# Revit family: Hemera_MIM_Mia-micro-suspension_R21
name_source: partatom
category: Lighting Fixtures
units: mm (PartAtom-declared; Revit-internal decimal feet)

## family parameters
Always vertical = Yes
Cut with Voids When Loaded = No
Host = Ceiling
Light Source = Yes
OmniClass Number = 23.80.70.11
OmniClass Title = Luminaries for Internal Lighting
Part Type = Normal
Room Calculation Point = No
Round Connector Dimension = Use Diameter
Shared = No

## types (240) — shared parameters
Color Filter = 16777215
Dimming Lamp Color Temperature Shift = <None>
Emit Shape Visible in Rendering = No
Emit from Circle Diameter = 50.8 mm  [stored 0.166667 ft]
HL_CanopyDiameter = 50.8 mm  [stored 0.166667 ft]
HL_CanopyHeigth = 6.35 mm  [stored 0.0208333 ft]
HL_CanopyRadius = 25.4 mm  [stored 0.0833333 ft]
HL_Frequency = 60 Hz
HL_LoadClassification = Eclairage
HL_Manufacturer = Hèmèra Inc.
HL_Model = MIA Micro-Suspension
HL_NumberofPoles = 1
HL_ProductCode = MIM
HL_URL = http://www.hemeralighting.org
Photometric Web File = MIM.IES
Tilt Angle = 90.00°
zero-valued in all types: Default Elevation

## per-type parameters (varying)
| type | HL_COC | HL_CableStart | HL_CordDiameter | HL_CylinderSize | HL_D010 | HL_FinishCable | HL_FinishCanopy | HL_FinishCylinder | HL_REM-MC |
| MIM-31-PWC-SM-COB-5W/90/35K-D010-UNV | No | 31.62 mm | 3.18 mm  [stored 0.0104331 ft] | 76.2 mm  [stored 0.25 ft] | Yes | PWC-Pearly white cord | 31-Polished nickel plated | 31-Polished nickel plated | No |
| MIM-31-PWC-MD-COB-5W/90/35K-D010-UNV | No | 31.62 mm | 3.18 mm  [stored 0.0104331 ft] | 165.1 mm  [stored 0.541667 ft] | Yes | PWC-Pearly white cord | 31-Polished nickel plated | 31-Polished nickel plated | No |
| MIM-31-PWC-LG-COB-5W/90/35K-D010-UNV | No | 31.62 mm | 3.18 mm  [stored 0.0104331 ft] | 317.5 mm | Yes | PWC-Pearly white cord | 31-Polished nickel plated | 31-Polished nickel plated | No |
| MIM-31-PWC-LG-COB-5W/90/35K-REM-MC-UNV | No | 15.88 mm  [stored 0.0520997 ft] | 3.18 mm  [stored 0.0104331 ft] | 317.5 mm | No | PWC-Pearly white cord | 31-Polished nickel plated | 31-Polished nickel plated | Yes |
| MIM-31-PWC-MD-COB-5W/90/35K-REM-MC-UNV | No | 15.88 mm  [stored 0.0520997 ft] | 3.18 mm  [stored 0.0104331 ft] | 165.1 mm  [stored 0.541667 ft] | No | PWC-Pearly white cord | 31-Polished nickel plated | 31-Polished nickel plated | Yes |
| MIM-31-PWC-SM-COB-5W/90/35K-REM-MC-UNV | No | 15.88 mm  [stored 0.0520997 ft] | 3.18 mm  [stored 0.0104331 ft] | 76.2 mm  [stored 0.25 ft] | No | PWC-Pearly white cord | 31-Polished nickel plated | 31-Polished nickel plated | Yes |
| MIM-24-SGC-SM-COB-5W/90/35K-REM-MC-UNV | No | 15.88 mm  [stored 0.0520997 ft] | 3.18 mm  [stored 0.0104331 ft] | 76.2 mm  [stored 0.25 ft] | No | SGC-Satin gold cord | 24-Brushed nickel plated | 24-Brushed nickel plated | Yes |
| MIM-24-SGC-MD-COB-5W/90/35K-REM-MC-UNV | No | 15.88 mm  [stored 0.0520997 ft] | 3.18 mm  [stored 0.0104331 ft] | 165.1 mm  [stored 0.541667 ft] | No | SGC-Satin gold cord | 24-Brushed nickel plated | 24-Brushed nickel plated | Yes |
| MIM-24-SGC-LG-COB-5W/90/35K-REM-MC-UNV | No | 15.88 mm  [stored 0.0520997 ft] | 3.18 mm  [stored 0.0104331 ft] | 317.5 mm | No | SGC-Satin gold cord | 24-Brushed nickel plated | 24-Brushed nickel plated | Yes |
| MIM-24-SGC-LG-COB-5W/90/35K-D010-UNV | No | 31.62 mm | 3.18 mm  [stored 0.0104331 ft] | 317.5 mm | Yes | SGC-Satin gold cord | 24-Brushed nickel plated | 24-Brushed nickel plated | No |
| MIM-24-SGC-MD-COB-5W/90/35K-D010-UNV | No | 31.62 mm | 3.18 mm  [stored 0.0104331 ft] | 165.1 mm  [stored 0.541667 ft] | Yes | SGC-Satin gold cord | 24-Brushed nickel plated | 24-Brushed nickel plated | No |
| MIM-24-SGC-SM-COB-5W/90/35K-D010-UNV | No | 31.62 mm | 3.18 mm  [stored 0.0104331 ft] | 76.2 mm  [stored 0.25 ft] | Yes | SGC-Satin gold cord | 24-Brushed nickel plated | 24-Brushed nickel plated | No |
| MIM-24-SBC-SM-COB-5W/90/35K-REM-MC-UNV | No | 15.88 mm  [stored 0.0520997 ft] | 3.18 mm  [stored 0.0104331 ft] | 76.2 mm  [stored 0.25 ft] | No | SBC-Silky black cord | 24-Brushed nickel plated | 24-Brushed nickel plated | Yes |
| MIM-24-SBC-MD-COB-5W/90/35K-REM-MC-UNV | No | 15.88 mm  [stored 0.0520997 ft] | 3.18 mm  [stored 0.0104331 ft] | 165.1 mm  [stored 0.541667 ft] | No | SBC-Silky black cord | 24-Brushed nickel plated | 24-Brushed nickel plated | Yes |
| MIM-24-SBC-LG-COB-5W/90/35K-REM-MC-UNV | No | 15.88 mm  [stored 0.0520997 ft] | 3.18 mm  [stored 0.0104331 ft] | 317.5 mm | No | SBC-Silky black cord | 24-Brushed nickel plated | 24-Brushed nickel plated | Yes |
| MIM-24-SBC-LG-COB-5W/90/35K-D010-UNV | No | 31.62 mm | 3.18 mm  [stored 0.0104331 ft] | 317.5 mm | Yes | SBC-Silky black cord | 24-Brushed nickel plated | 24-Brushed nickel plated | No |
| MIM-24-SBC-MD-COB-5W/90/35K-D010-UNV | No | 31.62 mm | 3.18 mm  [stored 0.0104331 ft] | 165.1 mm  [stored 0.541667 ft] | Yes | SBC-Silky black cord | 24-Brushed nickel plated | 24-Brushed nickel plated | No |
| MIM-24-SBC-SM-COB-5W/90/35K-D010-UNV | No | 31.62 mm | 3.18 mm  [stored 0.0104331 ft] | 76.2 mm  [stored 0.25 ft] | Yes | SBC-Silky black cord | 24-Brushed nickel plated | 24-Brushed nickel plated | No |
| MIM-24-COC-SM-COB-5W/90/35K-REM-MC-UNV | Yes | 15.88 mm  [stored 0.0520997 ft] | 1.59 mm  [stored 0.00521653 ft] | 76.2 mm  [stored 0.25 ft] | No | COC-Coaxial cable | 24-Brushed nickel plated | 24-Brushed nickel plated | Yes |
| MIM-24-COC-MD-COB-5W/90/35K-REM-MC-UNV | Yes | 15.88 mm  [stored 0.0520997 ft] | 1.59 mm  [stored 0.00521653 ft] | 165.1 mm  [stored 0.541667 ft] | No | COC-Coaxial cable | 24-Brushed nickel plated | 24-Brushed nickel plated | Yes |
| MIM-24-COC-LG-COB-5W/90/35K-REM-MC-UNV | Yes | 15.88 mm  [stored 0.0520997 ft] | 1.59 mm  [stored 0.00521653 ft] | 317.5 mm | No | COC-Coaxial cable | 24-Brushed nickel plated | 24-Brushed nickel plated | Yes |
| MIM-24-COC-LG-COB-5W/90/35K-D010-UNV | Yes | 31.62 mm | 1.59 mm  [stored 0.00521653 ft] | 317.5 mm | Yes | COC-Coaxial cable | 24-Brushed nickel plated | 24-Brushed nickel plated | No |
| MIM-24-COC-MD-COB-5W/90/35K-D010-UNV | Yes | 31.62 mm | 1.59 mm  [stored 0.00521653 ft] | 165.1 mm  [stored 0.541667 ft] | Yes | COC-Coaxial cable | 24-Brushed nickel plated | 24-Brushed nickel plated | No |
| MIM-24-COC-SM-COB-5W/90/35K-D010-UNV | Yes | 31.62 mm | 1.59 mm  [stored 0.00521653 ft] | 76.2 mm  [stored 0.25 ft] | Yes | COC-Coaxial cable | 24-Brushed nickel plated | 24-Brushed nickel plated | No |
| MIM-24-AGC-SM-COB-5W/90/35K-REM-MC-UNV | No | 15.88 mm  [stored 0.0520997 ft] | 3.18 mm  [stored 0.0104331 ft] | 76.2 mm  [stored 0.25 ft] | No | AGC-Anthracite gray cord | 24-Brushed nickel plated | 24-Brushed nickel plated | Yes |
| MIM-24-AGC-MD-COB-5W/90/35K-REM-MC-UNV | No | 15.88 mm  [stored 0.0520997 ft] | 3.18 mm  [stored 0.0104331 ft] | 165.1 mm  [stored 0.541667 ft] | No | AGC-Anthracite gray cord | 24-Brushed nickel plated | 24-Brushed nickel plated | Yes |
| MIM-24-AGC-LG-COB-5W/90/35K-REM-MC-UNV | No | 15.88 mm  [stored 0.0520997 ft] | 3.18 mm  [stored 0.0104331 ft] | 317.5 mm | No | AGC-Anthracite gray cord | 24-Brushed nickel plated | 24-Brushed nickel plated | Yes |
| MIM-24-AGC-LG-COB-5W/90/35K-D010-UNV | No | 31.62 mm | 3.18 mm  [stored 0.0104331 ft] | 317.5 mm | Yes | AGC-Anthracite gray cord | 24-Brushed nickel plated | 24-Brushed nickel plated | No |
| MIM-24-AGC-MD-COB-5W/90/35K-D010-UNV | No | 31.62 mm | 3.18 mm  [stored 0.0104331 ft] | 165.1 mm  [stored 0.541667 ft] | Yes | AGC-Anthracite gray cord | 24-Brushed nickel plated | 24-Brushed nickel plated | No |
| MIM-24-AGC-SM-COB-5W/90/35K-D010-UNV | No | 31.62 mm | 3.18 mm  [stored 0.0104331 ft] | 76.2 mm  [stored 0.25 ft] | Yes | AGC-Anthracite gray cord | 24-Brushed nickel plated | 24-Brushed nickel plated | No |
| MIM-24-PWC-SM-COB-5W/90/35K-REM-MC-UNV | No | 15.88 mm  [stored 0.0520997 ft] | 3.18 mm  [stored 0.0104331 ft] | 76.2 mm  [stored 0.25 ft] | No | PWC-Pearly white cord | 24-Brushed nickel plated | 24-Brushed nickel plated | Yes |
| MIM-24-PWC-MD-COB-5W/90/35K-REM-MC-UNV | No | 15.88 mm  [stored 0.0520997 ft] | 3.18 mm  [stored 0.0104331 ft] | 165.1 mm  [stored 0.541667 ft] | No | PWC-Pearly white cord | 24-Brushed nickel plated | 24-Brushed nickel plated | Yes |
| MIM-24-PWC-LG-COB-5W/90/35K-REM-MC-UNV | No | 15.88 mm  [stored 0.0520997 ft] | 3.18 mm  [stored 0.0104331 ft] | 317.5 mm | No | PWC-Pearly white cord | 24-Brushed nickel plated | 24-Brushed nickel plated | Yes |
| MIM-24-PWC-LG-COB-5W/90/35K-D010-UNV | No | 31.62 mm | 3.18 mm  [stored 0.0104331 ft] | 317.5 mm | Yes | PWC-Pearly white cord | 24-Brushed nickel plated | 24-Brushed nickel plated | No |
| MIM-24-PWC-MD-COB-5W/90/35K-D010-UNV | No | 31.62 mm | 3.18 mm  [stored 0.0104331 ft] | 165.1 mm  [stored 0.541667 ft] | Yes | PWC-Pearly white cord | 24-Brushed nickel plated | 24-Brushed nickel plated | No |
| MIM-24-PWC-SM-COB-5W/90/35K-D010-UNV | No | 31.62 mm | 3.18 mm  [stored 0.0104331 ft] | 76.2 mm  [stored 0.25 ft] | Yes | PWC-Pearly white cord | 24-Brushed nickel plated | 24-Brushed nickel plated | No |
| MIM-22-SGC-SM-COB-5W/90/35K-REM-MC-UNV | No | 15.88 mm  [stored 0.0520997 ft] | 3.18 mm  [stored 0.0104331 ft] | 76.2 mm  [stored 0.25 ft] | No | SGC-Satin gold cord | 22-Brushed gold plated | 22-Brushed gold plated | Yes |
| MIM-22-SGC-MD-COB-5W/90/35K-REM-MC-UNV | No | 15.88 mm  [stored 0.0520997 ft] | 3.18 mm  [stored 0.0104331 ft] | 165.1 mm  [stored 0.541667 ft] | No | SGC-Satin gold cord | 22-Brushed gold plated | 22-Brushed gold plated | Yes |
| MIM-22-SGC-LG-COB-5W/90/35K-REM-MC-UNV | No | 15.88 mm  [stored 0.0520997 ft] | 3.18 mm  [stored 0.0104331 ft] | 317.5 mm | No | SGC-Satin gold cord | 22-Brushed gold plated | 22-Brushed gold plated | Yes |
| MIM-22-SGC-LG-COB-5W/90/35K-D010-UNV | No | 31.62 mm | 3.18 mm  [stored 0.0104331 ft] | 317.5 mm | Yes | SGC-Satin gold cord | 22-Brushed gold plated | 22-Brushed gold plated | No |
| MIM-22-SGC-MD-COB-5W/90/35K-D010-UNV | No | 31.62 mm | 3.18 mm  [stored 0.0104331 ft] | 165.1 mm  [stored 0.541667 ft] | Yes | SGC-Satin gold cord | 22-Brushed gold plated | 22-Brushed gold plated | No |
| MIM-22-SGC-SM-COB-5W/90/35K-D010-UNV | No | 31.62 mm | 3.18 mm  [stored 0.0104331 ft] | 76.2 mm  [stored 0.25 ft] | Yes | SGC-Satin gold cord | 22-Brushed gold plated | 22-Brushed gold plated | No |
| MIM-22-SBC-SM-COB-5W/90/35K-REM-MC-UNV | No | 15.88 mm  [stored 0.0520997 ft] | 3.18 mm  [stored 0.0104331 ft] | 76.2 mm  [stored 0.25 ft] | No | SBC-Silky black cord | 22-Brushed gold plated | 22-Brushed gold plated | Yes |
| MIM-22-SBC-MD-COB-5W/90/35K-REM-MC-UNV | No | 15.88 mm  [stored 0.0520997 ft] | 3.18 mm  [stored 0.0104331 ft] | 165.1 mm  [stored 0.541667 ft] | No | SBC-Silky black cord | 22-Brushed gold plated | 22-Brushed gold plated | Yes |
| MIM-22-SBC-LG-COB-5W/90/35K-REM-MC-UNV | No | 15.88 mm  [stored 0.0520997 ft] | 3.18 mm  [stored 0.0104331 ft] | 317.5 mm | No | SBC-Silky black cord | 22-Brushed gold plated | 22-Brushed gold plated | Yes |
| MIM-22-SBC-LG-COB-5W/90/35K-D010-UNV | No | 31.62 mm | 3.18 mm  [stored 0.0104331 ft] | 317.5 mm | Yes | SBC-Silky black cord | 22-Brushed gold plated | 22-Brushed gold plated | No |
| MIM-22-SBC-MD-COB-5W/90/35K-D010-UNV | No | 31.62 mm | 3.18 mm  [stored 0.0104331 ft] | 165.1 mm  [stored 0.541667 ft] | Yes | SBC-Silky black cord | 22-Brushed gold plated | 22-Brushed gold plated | No |
| MIM-22-SBC-SM-COB-5W/90/35K-D010-UNV | No | 31.62 mm | 3.18 mm  [stored 0.0104331 ft] | 76.2 mm  [stored 0.25 ft] | Yes | SBC-Silky black cord | 22-Brushed gold plated | 22-Brushed gold plated | No |
| MIM-22-COC-SM-COB-5W/90/35K-REM-MC-UNV | Yes | 15.88 mm  [stored 0.0520997 ft] | 1.59 mm  [stored 0.00521653 ft] | 76.2 mm  [stored 0.25 ft] | No | COC-Coaxial cable | 22-Brushed gold plated | 22-Brushed gold plated | Yes |
| MIM-22-COC-MD-COB-5W/90/35K-REM-MC-UNV | Yes | 15.88 mm  [stored 0.0520997 ft] | 1.59 mm  [stored 0.00521653 ft] | 165.1 mm  [stored 0.541667 ft] | No | COC-Coaxial cable | 22-Brushed gold plated | 22-Brushed gold plated | Yes |
| MIM-22-COC-LG-COB-5W/90/35K-REM-MC-UNV | Yes | 15.88 mm  [stored 0.0520997 ft] | 1.59 mm  [stored 0.00521653 ft] | 317.5 mm | No | COC-Coaxial cable | 22-Brushed gold plated | 22-Brushed gold plated | Yes |
| MIM-22-COC-LG-COB-5W/90/35K-D010-UNV | Yes | 31.62 mm | 1.59 mm  [stored 0.00521653 ft] | 317.5 mm | Yes | COC-Coaxial cable | 22-Brushed gold plated | 22-Brushed gold plated | No |
| MIM-22-COC-MD-COB-5W/90/35K-D010-UNV | Yes | 31.62 mm | 1.59 mm  [stored 0.00521653 ft] | 165.1 mm  [stored 0.541667 ft] | Yes | COC-Coaxial cable | 22-Brushed gold plated | 22-Brushed gold plated | No |
| MIM-22-COC-SM-COB-5W/90/35K-D010-UNV | Yes | 31.62 mm | 1.59 mm  [stored 0.00521653 ft] | 76.2 mm  [stored 0.25 ft] | Yes | COC-Coaxial cable | 22-Brushed gold plated | 22-Brushed gold plated | No |
| MIM-22-AGC-SM-COB-5W/90/35K-REM-MC-UNV | No | 15.88 mm  [stored 0.0520997 ft] | 3.18 mm  [stored 0.0104331 ft] | 76.2 mm  [stored 0.25 ft] | No | AGC-Anthracite gray cord | 22-Brushed gold plated | 22-Brushed gold plated | Yes |
| MIM-22-AGC-MD-COB-5W/90/35K-REM-MC-UNV | No | 15.88 mm  [stored 0.0520997 ft] | 3.18 mm  [stored 0.0104331 ft] | 165.1 mm  [stored 0.541667 ft] | No | AGC-Anthracite gray cord | 22-Brushed gold plated | 22-Brushed gold plated | Yes |
| MIM-22-AGC-LG-COB-5W/90/35K-REM-MC-UNV | No | 15.88 mm  [stored 0.0520997 ft] | 3.18 mm  [stored 0.0104331 ft] | 317.5 mm | No | AGC-Anthracite gray cord | 22-Brushed gold plated | 22-Brushed gold plated | Yes |
| MIM-22-AGC-LG-COB-5W/90/35K-D010-UNV | No | 31.62 mm | 3.18 mm  [stored 0.0104331 ft] | 317.5 mm | Yes | AGC-Anthracite gray cord | 22-Brushed gold plated | 22-Brushed gold plated | No |
| MIM-22-AGC-MD-COB-5W/90/35K-D010-UNV | No | 31.62 mm | 3.18 mm  [stored 0.0104331 ft] | 165.1 mm  [stored 0.541667 ft] | Yes | AGC-Anthracite gray cord | 22-Brushed gold plated | 22-Brushed gold plated | No |
| MIM-22-AGC-SM-COB-5W/90/35K-D010-UNV | No | 31.62 mm | 3.18 mm  [stored 0.0104331 ft] | 76.2 mm  [stored 0.25 ft] | Yes | AGC-Anthracite gray cord | 22-Brushed gold plated | 22-Brushed gold plated | No |
| MIM-22-PWC-SM-COB-5W/90/35K-REM-MC-UNV | No | 15.88 mm  [stored 0.0520997 ft] | 3.18 mm  [stored 0.0104331 ft] | 76.2 mm  [stored 0.25 ft] | No | PWC-Pearly white cord | 22-Brushed gold plated | 22-Brushed gold plated | Yes |
| MIM-22-PWC-MD-COB-5W/90/35K-REM-MC-UNV | No | 15.88 mm  [stored 0.0520997 ft] | 3.18 mm  [stored 0.0104331 ft] | 165.1 mm  [stored 0.541667 ft] | No | PWC-Pearly white cord | 22-Brushed gold plated | 22-Brushed gold plated | Yes |
| MIM-22-PWC-LG-COB-5W/90/35K-REM-MC-UNV | No | 15.88 mm  [stored 0.0520997 ft] | 3.18 mm  [stored 0.0104331 ft] | 317.5 mm | No | PWC-Pearly white cord | 22-Brushed gold plated | 22-Brushed gold plated | Yes |
| MIM-22-PWC-LG-COB-5W/90/35K-D010-UNV | No | 31.62 mm | 3.18 mm  [stored 0.0104331 ft] | 317.5 mm | Yes | PWC-Pearly white cord | 22-Brushed gold plated | 22-Brushed gold plated | No |
| MIM-22-PWC-MD-COB-5W/90/35K-D010-UNV | No | 31.62 mm | 3.18 mm  [stored 0.0104331 ft] | 165.1 mm  [stored 0.541667 ft] | Yes | PWC-Pearly white cord | 22-Brushed gold plated | 22-Brushed gold plated | No |
| MIM-22-PWC-SM-COB-5W/90/35K-D010-UNV | No | 31.62 mm | 3.18 mm  [stored 0.0104331 ft] | 76.2 mm  [stored 0.25 ft] | Yes | PWC-Pearly white cord | 22-Brushed gold plated | 22-Brushed gold plated | No |
| MIM-21-SGC-SM-COB-5W/90/35K-REM-MC-UNV | No | 15.88 mm  [stored 0.0520997 ft] | 3.18 mm  [stored 0.0104331 ft] | 76.2 mm  [stored 0.25 ft] | No | SGC-Satin gold cord | 21-Polished gold plated | 21-Polished gold plated | Yes |
| MIM-21-SGC-MD-COB-5W/90/35K-REM-MC-UNV | No | 15.88 mm  [stored 0.0520997 ft] | 3.18 mm  [stored 0.0104331 ft] | 165.1 mm  [stored 0.541667 ft] | No | SGC-Satin gold cord | 21-Polished gold plated | 21-Polished gold plated | Yes |
| MIM-21-SGC-LG-COB-5W/90/35K-REM-MC-UNV | No | 15.88 mm  [stored 0.0520997 ft] | 3.18 mm  [stored 0.0104331 ft] | 317.5 mm | No | SGC-Satin gold cord | 21-Polished gold plated | 21-Polished gold plated | Yes |
| MIM-21-SGC-LG-COB-5W/90/35K-D010-UNV | No | 31.62 mm | 3.18 mm  [stored 0.0104331 ft] | 317.5 mm | Yes | SGC-Satin gold cord | 21-Polished gold plated | 21-Polished gold plated | No |
| MIM-21-SGC-MD-COB-5W/90/35K-D010-UNV | No | 31.62 mm | 3.18 mm  [stored 0.0104331 ft] | 165.1 mm  [stored 0.541667 ft] | Yes | SGC-Satin gold cord | 21-Polished gold plated | 21-Polished gold plated | No |
| MIM-21-SGC-SM-COB-5W/90/35K-D010-UNV | No | 31.62 mm | 3.18 mm  [stored 0.0104331 ft] | 76.2 mm  [stored 0.25 ft] | Yes | SGC-Satin gold cord | 21-Polished gold plated | 21-Polished gold plated | No |
| MIM-21-SBC-SM-COB-5W/90/35K-REM-MC-UNV | No | 15.88 mm  [stored 0.0520997 ft] | 3.18 mm  [stored 0.0104331 ft] | 76.2 mm  [stored 0.25 ft] | No | SBC-Silky black cord | 21-Polished gold plated | 21-Polished gold plated | Yes |
| MIM-21-SBC-MD-COB-5W/90/35K-REM-MC-UNV | No | 15.88 mm  [stored 0.0520997 ft] | 3.18 mm  [stored 0.0104331 ft] | 165.1 mm  [stored 0.541667 ft] | No | SBC-Silky black cord | 21-Polished gold plated | 21-Polished gold plated | Yes |
| MIM-21-SBC-LG-COB-5W/90/35K-REM-MC-UNV | No | 15.88 mm  [stored 0.0520997 ft] | 3.18 mm  [stored 0.0104331 ft] | 317.5 mm | No | SBC-Silky black cord | 21-Polished gold plated | 21-Polished gold plated | Yes |
| MIM-21-SBC-LG-COB-5W/90/35K-D010-UNV | No | 31.62 mm | 3.18 mm  [stored 0.0104331 ft] | 317.5 mm | Yes | SBC-Silky black cord | 21-Polished gold plated | 21-Polished gold plated | No |
| MIM-21-SBC-MD-COB-5W/90/35K-D010-UNV | No | 31.62 mm | 3.18 mm  [stored 0.0104331 ft] | 165.1 mm  [stored 0.541667 ft] | Yes | SBC-Silky black cord | 21-Polished gold plated | 21-Polished gold plated | No |
| MIM-21-SBC-SM-COB-5W/90/35K-D010-UNV | No | 31.62 mm | 3.18 mm  [stored 0.0104331 ft] | 76.2 mm  [stored 0.25 ft] | Yes | SBC-Silky black cord | 21-Polished gold plated | 21-Polished gold plated | No |
| MIM-21-COC-SM-COB-5W/90/35K-REM-MC-UNV | Yes | 15.88 mm  [stored 0.0520997 ft] | 1.59 mm  [stored 0.00521653 ft] | 76.2 mm  [stored 0.25 ft] | No | COC-Coaxial cable | 21-Polished gold plated | 21-Polished gold plated | Yes |
| MIM-21-COC-MD-COB-5W/90/35K-REM-MC-UNV | Yes | 15.88 mm  [stored 0.0520997 ft] | 1.59 mm  [stored 0.00521653 ft] | 165.1 mm  [stored 0.541667 ft] | No | COC-Coaxial cable | 21-Polished gold plated | 21-Polished gold plated | Yes |
| MIM-21-COC-LG-COB-5W/90/35K-REM-MC-UNV | Yes | 15.88 mm  [stored 0.0520997 ft] | 1.59 mm  [stored 0.00521653 ft] | 317.5 mm | No | COC-Coaxial cable | 21-Polished gold plated | 21-Polished gold plated | Yes |
| MIM-21-COC-LG-COB-5W/90/35K-D010-UNV | Yes | 31.62 mm | 1.59 mm  [stored 0.00521653 ft] | 317.5 mm | Yes | COC-Coaxial cable | 21-Polished gold plated | 21-Polished gold plated | No |
| MIM-21-COC-MD-COB-5W/90/35K-D010-UNV | Yes | 31.62 mm | 1.59 mm  [stored 0.00521653 ft] | 165.1 mm  [stored 0.541667 ft] | Yes | COC-Coaxial cable | 21-Polished gold plated | 21-Polished gold plated | No |
| MIM-21-COC-SM-COB-5W/90/35K-D010-UNV | Yes | 31.62 mm | 1.59 mm  [stored 0.00521653 ft] | 76.2 mm  [stored 0.25 ft] | Yes | COC-Coaxial cable | 21-Polished gold plated | 21-Polished gold plated | No |
| MIM-21-AGC-SM-COB-5W/90/35K-REM-MC-UNV | No | 15.88 mm  [stored 0.0520997 ft] | 3.18 mm  [stored 0.0104331 ft] | 76.2 mm  [stored 0.25 ft] | No | AGC-Anthracite gray cord | 21-Polished gold plated | 21-Polished gold plated | Yes |
| MIM-21-AGC-MD-COB-5W/90/35K-REM-MC-UNV | No | 15.88 mm  [stored 0.0520997 ft] | 3.18 mm  [stored 0.0104331 ft] | 165.1 mm  [stored 0.541667 ft] | No | AGC-Anthracite gray cord | 21-Polished gold plated | 21-Polished gold plated | Yes |
| MIM-21-AGC-LG-COB-5W/90/35K-REM-MC-UNV | No | 15.88 mm  [stored 0.0520997 ft] | 3.18 mm  [stored 0.0104331 ft] | 317.5 mm | No | AGC-Anthracite gray cord | 21-Polished gold plated | 21-Polished gold plated | Yes |
| MIM-21-AGC-LG-COB-5W/90/35K-D010-UNV | No | 31.62 mm | 3.18 mm  [stored 0.0104331 ft] | 317.5 mm | Yes | AGC-Anthracite gray cord | 21-Polished gold plated | 21-Polished gold plated | No |
| MIM-21-AGC-MD-COB-5W/90/35K-D010-UNV | No | 31.62 mm | 3.18 mm  [stored 0.0104331 ft] | 165.1 mm  [stored 0.541667 ft] | Yes | AGC-Anthracite gray cord | 21-Polished gold plated | 21-Polished gold plated | No |
| MIM-21-AGC-SM-COB-5W/90/35K-D010-UNV | No | 31.62 mm | 3.18 mm  [stored 0.0104331 ft] | 76.2 mm  [stored 0.25 ft] | Yes | AGC-Anthracite gray cord | 21-Polished gold plated | 21-Polished gold plated | No |
| MIM-21-PWC-SM-COB-5W/90/35K-REM-MC-UNV | No | 15.88 mm  [stored 0.0520997 ft] | 3.18 mm  [stored 0.0104331 ft] | 76.2 mm  [stored 0.25 ft] | No | PWC-Pearly white cord | 21-Polished gold plated | 21-Polished gold plated | Yes |
| MIM-21-PWC-MD-COB-5W/90/35K-REM-MC-UNV | No | 15.88 mm  [stored 0.0520997 ft] | 3.18 mm  [stored 0.0104331 ft] | 165.1 mm  [stored 0.541667 ft] | No | PWC-Pearly white cord | 21-Polished gold plated | 21-Polished gold plated | Yes |
| MIM-21-PWC-LG-COB-5W/90/35K-REM-MC-UNV | No | 15.88 mm  [stored 0.0520997 ft] | 3.18 mm  [stored 0.0104331 ft] | 317.5 mm | No | PWC-Pearly white cord | 21-Polished gold plated | 21-Polished gold plated | Yes |
| MIM-21-PWC-LG-COB-5W/90/35K-D010-UNV | No | 31.62 mm | 3.18 mm  [stored 0.0104331 ft] | 317.5 mm | Yes | PWC-Pearly white cord | 21-Polished gold plated | 21-Polished gold plated | No |
| MIM-21-PWC-MD-COB-5W/90/35K-D010-UNV | No | 31.62 mm | 3.18 mm  [stored 0.0104331 ft] | 165.1 mm  [stored 0.541667 ft] | Yes | PWC-Pearly white cord | 21-Polished gold plated | 21-Polished gold plated | No |
| MIM-21-PWC-SM-COB-5W/90/35K-D010-UNV | No | 31.62 mm | 3.18 mm  [stored 0.0104331 ft] | 76.2 mm  [stored 0.25 ft] | Yes | PWC-Pearly white cord | 21-Polished gold plated | 21-Polished gold plated | No |
| MIM-08-SGC-SM-COB-5W/90/35K-REM-MC-UNV | No | 15.88 mm  [stored 0.0520997 ft] | 3.18 mm  [stored 0.0104331 ft] | 76.2 mm  [stored 0.25 ft] | No | SGC-Satin gold cord | 08-Dark mat bronze painted | 08-Dark mat bronze painted | Yes |
| MIM-08-SGC-MD-COB-5W/90/35K-REM-MC-UNV | No | 15.88 mm  [stored 0.0520997 ft] | 3.18 mm  [stored 0.0104331 ft] | 165.1 mm  [stored 0.541667 ft] | No | SGC-Satin gold cord | 08-Dark mat bronze painted | 08-Dark mat bronze painted | Yes |
| MIM-08-SGC-LG-COB-5W/90/35K-REM-MC-UNV | No | 15.88 mm  [stored 0.0520997 ft] | 3.18 mm  [stored 0.0104331 ft] | 317.5 mm | No | SGC-Satin gold cord | 08-Dark mat bronze painted | 08-Dark mat bronze painted | Yes |
| MIM-08-SGC-LG-COB-5W/90/35K-D010-UNV | No | 31.62 mm | 3.18 mm  [stored 0.0104331 ft] | 317.5 mm | Yes | SGC-Satin gold cord | 08-Dark mat bronze painted | 08-Dark mat bronze painted | No |
| MIM-08-SGC-MD-COB-5W/90/35K-D010-UNV | No | 31.62 mm | 3.18 mm  [stored 0.0104331 ft] | 165.1 mm  [stored 0.541667 ft] | Yes | SGC-Satin gold cord | 08-Dark mat bronze painted | 08-Dark mat bronze painted | No |
| MIM-08-SGC-SM-COB-5W/90/35K-D010-UNV | No | 31.62 mm | 3.18 mm  [stored 0.0104331 ft] | 76.2 mm  [stored 0.25 ft] | Yes | SGC-Satin gold cord | 08-Dark mat bronze painted | 08-Dark mat bronze painted | No |
| MIM-08-SBC-SM-COB-5W/90/35K-REM-MC-UNV | No | 15.88 mm  [stored 0.0520997 ft] | 3.18 mm  [stored 0.0104331 ft] | 76.2 mm  [stored 0.25 ft] | No | SBC-Silky black cord | 08-Dark mat bronze painted | 08-Dark mat bronze painted | Yes |
| MIM-08-SBC-MD-COB-5W/90/35K-REM-MC-UNV | No | 15.88 mm  [stored 0.0520997 ft] | 3.18 mm  [stored 0.0104331 ft] | 165.1 mm  [stored 0.541667 ft] | No | SBC-Silky black cord | 08-Dark mat bronze painted | 08-Dark mat bronze painted | Yes |
| MIM-08-SBC-LG-COB-5W/90/35K-REM-MC-UNV | No | 15.88 mm  [stored 0.0520997 ft] | 3.18 mm  [stored 0.0104331 ft] | 317.5 mm | No | SBC-Silky black cord | 08-Dark mat bronze painted | 08-Dark mat bronze painted | Yes |
| MIM-08-SBC-LG-COB-5W/90/35K-D010-UNV | No | 31.62 mm | 3.18 mm  [stored 0.0104331 ft] | 317.5 mm | Yes | SBC-Silky black cord | 08-Dark mat bronze painted | 08-Dark mat bronze painted | No |
| MIM-08-SBC-MD-COB-5W/90/35K-D010-UNV | No | 31.62 mm | 3.18 mm  [stored 0.0104331 ft] | 165.1 mm  [stored 0.541667 ft] | Yes | SBC-Silky black cord | 08-Dark mat bronze painted | 08-Dark mat bronze painted | No |
| MIM-08-SBC-SM-COB-5W/90/35K-D010-UNV | No | 31.62 mm | 3.18 mm  [stored 0.0104331 ft] | 76.2 mm  [stored 0.25 ft] | Yes | SBC-Silky black cord | 08-Dark mat bronze painted | 08-Dark mat bronze painted | No |
| MIM-08-COC-SM-COB-5W/90/35K-REM-MC-UNV | Yes | 15.88 mm  [stored 0.0520997 ft] | 1.59 mm  [stored 0.00521653 ft] | 76.2 mm  [stored 0.25 ft] | No | COC-Coaxial cable | 08-Dark mat bronze painted | 08-Dark mat bronze painted | Yes |
| MIM-08-COC-MD-COB-5W/90/35K-REM-MC-UNV | Yes | 15.88 mm  [stored 0.0520997 ft] | 1.59 mm  [stored 0.00521653 ft] | 165.1 mm  [stored 0.541667 ft] | No | COC-Coaxial cable | 08-Dark mat bronze painted | 08-Dark mat bronze painted | Yes |
| MIM-08-COC-LG-COB-5W/90/35K-REM-MC-UNV | Yes | 15.88 mm  [stored 0.0520997 ft] | 1.59 mm  [stored 0.00521653 ft] | 317.5 mm | No | COC-Coaxial cable | 08-Dark mat bronze painted | 08-Dark mat bronze painted | Yes |
| MIM-08-COC-LG-COB-5W/90/35K-D010-UNV | Yes | 31.62 mm | 1.59 mm  [stored 0.00521653 ft] | 317.5 mm | Yes | COC-Coaxial cable | 08-Dark mat bronze painted | 08-Dark mat bronze painted | No |
| MIM-08-COC-MD-COB-5W/90/35K-D010-UNV | Yes | 31.62 mm | 1.59 mm  [stored 0.00521653 ft] | 165.1 mm  [stored 0.541667 ft] | Yes | COC-Coaxial cable | 08-Dark mat bronze painted | 08-Dark mat bronze painted | No |
| MIM-08-COC-SM-COB-5W/90/35K-D010-UNV | Yes | 31.62 mm | 1.59 mm  [stored 0.00521653 ft] | 76.2 mm  [stored 0.25 ft] | Yes | COC-Coaxial cable | 08-Dark mat bronze painted | 08-Dark mat bronze painted | No |
| MIM-08-AGC-SM-COB-5W/90/35K-REM-MC-UNV | No | 15.88 mm  [stored 0.0520997 ft] | 3.18 mm  [stored 0.0104331 ft] | 76.2 mm  [stored 0.25 ft] | No | AGC-Anthracite gray cord | 08-Dark mat bronze painted | 08-Dark mat bronze painted | Yes |
| MIM-08-AGC-MD-COB-5W/90/35K-REM-MC-UNV | No | 15.88 mm  [stored 0.0520997 ft] | 3.18 mm  [stored 0.0104331 ft] | 165.1 mm  [stored 0.541667 ft] | No | AGC-Anthracite gray cord | 08-Dark mat bronze painted | 08-Dark mat bronze painted | Yes |
| MIM-08-AGC-LG-COB-5W/90/35K-REM-MC-UNV | No | 15.88 mm  [stored 0.0520997 ft] | 3.18 mm  [stored 0.0104331 ft] | 317.5 mm | No | AGC-Anthracite gray cord | 08-Dark mat bronze painted | 08-Dark mat bronze painted | Yes |
| MIM-08-AGC-LG-COB-5W/90/35K-D010-UNV | No | 31.62 mm | 3.18 mm  [stored 0.0104331 ft] | 317.5 mm | Yes | AGC-Anthracite gray cord | 08-Dark mat bronze painted | 08-Dark mat bronze painted | No |
| MIM-08-AGC-MD-COB-5W/90/35K-D010-UNV | No | 31.62 mm | 3.18 mm  [stored 0.0104331 ft] | 165.1 mm  [stored 0.541667 ft] | Yes | AGC-Anthracite gray cord | 08-Dark mat bronze painted | 08-Dark mat bronze painted | No |
| MIM-08-AGC-SM-COB-5W/90/35K-D010-UNV | No | 31.62 mm | 3.18 mm  [stored 0.0104331 ft] | 76.2 mm  [stored 0.25 ft] | Yes | AGC-Anthracite gray cord | 08-Dark mat bronze painted | 08-Dark mat bronze painted | No |
| MIM-08-PWC-SM-COB-5W/90/35K-REM-MC-UNV | No | 15.88 mm  [stored 0.0520997 ft] | 3.18 mm  [stored 0.0104331 ft] | 76.2 mm  [stored 0.25 ft] | No | PWC-Pearly white cord | 08-Dark mat bronze painted | 08-Dark mat bronze painted | Yes |
| MIM-08-PWC-MD-COB-5W/90/35K-REM-MC-UNV | No | 15.88 mm  [stored 0.0520997 ft] | 3.18 mm  [stored 0.0104331 ft] | 165.1 mm  [stored 0.541667 ft] | No | PWC-Pearly white cord | 08-Dark mat bronze painted | 08-Dark mat bronze painted | Yes |
| MIM-08-PWC-LG-COB-5W/90/35K-REM-MC-UNV | No | 15.88 mm  [stored 0.0520997 ft] | 3.18 mm  [stored 0.0104331 ft] | 317.5 mm | No | PWC-Pearly white cord | 08-Dark mat bronze painted | 08-Dark mat bronze painted | Yes |
| MIM-08-PWC-LG-COB-5W/90/35K-D010-UNV | No | 31.62 mm | 3.18 mm  [stored 0.0104331 ft] | 317.5 mm | Yes | PWC-Pearly white cord | 08-Dark mat bronze painted | 08-Dark mat bronze painted | No |
| MIM-08-PWC-MD-COB-5W/90/35K-D010-UNV | No | 31.62 mm | 3.18 mm  [stored 0.0104331 ft] | 165.1 mm  [stored 0.541667 ft] | Yes | PWC-Pearly white cord | 08-Dark mat bronze painted | 08-Dark mat bronze painted | No |
| MIM-08-PWC-SM-COB-5W/90/35K-D010-UNV | No | 31.62 mm | 3.18 mm  [stored 0.0104331 ft] | 76.2 mm  [stored 0.25 ft] | Yes | PWC-Pearly white cord | 08-Dark mat bronze painted | 08-Dark mat bronze painted | No |
| MIM-03-SGC-SM-COB-5W/90/35K-REM-MC-UNV | No | 15.88 mm  [stored 0.0520997 ft] | 3.18 mm  [stored 0.0104331 ft] | 76.2 mm  [stored 0.25 ft] | No | SGC-Satin gold cord | 03-Warm dark grey painted | 03-Warm dark grey painted | Yes |
| MIM-03-SGC-MD-COB-5W/90/35K-REM-MC-UNV | No | 15.88 mm  [stored 0.0520997 ft] | 3.18 mm  [stored 0.0104331 ft] | 165.1 mm  [stored 0.541667 ft] | No | SGC-Satin gold cord | 03-Warm dark grey painted | 03-Warm dark grey painted | Yes |
| MIM-03-SGC-LG-COB-5W/90/35K-REM-MC-UNV | No | 15.88 mm  [stored 0.0520997 ft] | 3.18 mm  [stored 0.0104331 ft] | 317.5 mm | No | SGC-Satin gold cord | 03-Warm dark grey painted | 03-Warm dark grey painted | Yes |
| MIM-03-SGC-LG-COB-5W/90/35K-D010-UNV | No | 31.62 mm | 3.18 mm  [stored 0.0104331 ft] | 317.5 mm | Yes | SGC-Satin gold cord | 03-Warm dark grey painted | 03-Warm dark grey painted | No |
| MIM-03-SGC-MD-COB-5W/90/35K-D010-UNV | No | 31.62 mm | 3.18 mm  [stored 0.0104331 ft] | 165.1 mm  [stored 0.541667 ft] | Yes | SGC-Satin gold cord | 03-Warm dark grey painted | 03-Warm dark grey painted | No |
| MIM-03-SGC-SM-COB-5W/90/35K-D010-UNV | No | 31.62 mm | 3.18 mm  [stored 0.0104331 ft] | 76.2 mm  [stored 0.25 ft] | Yes | SGC-Satin gold cord | 03-Warm dark grey painted | 03-Warm dark grey painted | No |
| MIM-03-SBC-SM-COB-5W/90/35K-REM-MC-UNV | No | 15.88 mm  [stored 0.0520997 ft] | 3.18 mm  [stored 0.0104331 ft] | 76.2 mm  [stored 0.25 ft] | No | SBC-Silky black cord | 03-Warm dark grey painted | 03-Warm dark grey painted | Yes |
| MIM-03-SBC-MD-COB-5W/90/35K-REM-MC-UNV | No | 15.88 mm  [stored 0.0520997 ft] | 3.18 mm  [stored 0.0104331 ft] | 165.1 mm  [stored 0.541667 ft] | No | SBC-Silky black cord | 03-Warm dark grey painted | 03-Warm dark grey painted | Yes |
| MIM-03-SBC-LG-COB-5W/90/35K-REM-MC-UNV | No | 15.88 mm  [stored 0.0520997 ft] | 3.18 mm  [stored 0.0104331 ft] | 317.5 mm | No | SBC-Silky black cord | 03-Warm dark grey painted | 03-Warm dark grey painted | Yes |
| MIM-03-SBC-LG-COB-5W/90/35K-D010-UNV | No | 31.62 mm | 3.18 mm  [stored 0.0104331 ft] | 317.5 mm | Yes | SBC-Silky black cord | 03-Warm dark grey painted | 03-Warm dark grey painted | No |
| MIM-03-SBC-MD-COB-5W/90/35K-D010-UNV | No | 31.62 mm | 3.18 mm  [stored 0.0104331 ft] | 165.1 mm  [stored 0.541667 ft] | Yes | SBC-Silky black cord | 03-Warm dark grey painted | 03-Warm dark grey painted | No |
| MIM-03-SBC-SM-COB-5W/90/35K-D010-UNV | No | 31.62 mm | 3.18 mm  [stored 0.0104331 ft] | 76.2 mm  [stored 0.25 ft] | Yes | SBC-Silky black cord | 03-Warm dark grey painted | 03-Warm dark grey painted | No |
| MIM-03-COC-SM-COB-5W/90/35K-REM-MC-UNV | Yes | 15.88 mm  [stored 0.0520997 ft] | 1.59 mm  [stored 0.00521653 ft] | 76.2 mm  [stored 0.25 ft] | No | COC-Coaxial cable | 03-Warm dark grey painted | 03-Warm dark grey painted | Yes |
| MIM-03-COC-MD-COB-5W/90/35K-REM-MC-UNV | Yes | 15.88 mm  [stored 0.0520997 ft] | 1.59 mm  [stored 0.00521653 ft] | 165.1 mm  [stored 0.541667 ft] | No | COC-Coaxial cable | 03-Warm dark grey painted | 03-Warm dark grey painted | Yes |
| MIM-03-COC-LG-COB-5W/90/35K-REM-MC-UNV | Yes | 15.88 mm  [stored 0.0520997 ft] | 1.59 mm  [stored 0.00521653 ft] | 317.5 mm | No | COC-Coaxial cable | 03-Warm dark grey painted | 03-Warm dark grey painted | Yes |
| MIM-03-COC-LG-COB-5W/90/35K-D010-UNV | Yes | 31.62 mm | 1.59 mm  [stored 0.00521653 ft] | 317.5 mm | Yes | COC-Coaxial cable | 03-Warm dark grey painted | 03-Warm dark grey painted | No |
| MIM-03-COC-MD-COB-5W/90/35K-D010-UNV | Yes | 31.62 mm | 1.59 mm  [stored 0.00521653 ft] | 165.1 mm  [stored 0.541667 ft] | Yes | COC-Coaxial cable | 03-Warm dark grey painted | 03-Warm dark grey painted | No |
| MIM-03-COC-SM-COB-5W/90/35K-D010-UNV | Yes | 31.62 mm | 1.59 mm  [stored 0.00521653 ft] | 76.2 mm  [stored 0.25 ft] | Yes | COC-Coaxial cable | 03-Warm dark grey painted | 03-Warm dark grey painted | No |
| MIM-03-AGC-SM-COB-5W/90/35K-REM-MC-UNV | No | 15.88 mm  [stored 0.0520997 ft] | 3.18 mm  [stored 0.0104331 ft] | 76.2 mm  [stored 0.25 ft] | No | AGC-Anthracite gray cord | 03-Warm dark grey painted | 03-Warm dark grey painted | Yes |
| MIM-03-AGC-MD-COB-5W/90/35K-REM-MC-UNV | No | 15.88 mm  [stored 0.0520997 ft] | 3.18 mm  [stored 0.0104331 ft] | 165.1 mm  [stored 0.541667 ft] | No | AGC-Anthracite gray cord | 03-Warm dark grey painted | 03-Warm dark grey painted | Yes |
| MIM-03-AGC-LG-COB-5W/90/35K-REM-MC-UNV | No | 15.88 mm  [stored 0.0520997 ft] | 3.18 mm  [stored 0.0104331 ft] | 317.5 mm | No | AGC-Anthracite gray cord | 03-Warm dark grey painted | 03-Warm dark grey painted | Yes |
| MIM-03-AGC-LG-COB-5W/90/35K-D010-UNV | No | 31.62 mm | 3.18 mm  [stored 0.0104331 ft] | 317.5 mm | Yes | AGC-Anthracite gray cord | 03-Warm dark grey painted | 03-Warm dark grey painted | No |
| MIM-03-AGC-MD-COB-5W/90/35K-D010-UNV | No | 31.62 mm | 3.18 mm  [stored 0.0104331 ft] | 165.1 mm  [stored 0.541667 ft] | Yes | AGC-Anthracite gray cord | 03-Warm dark grey painted | 03-Warm dark grey painted | No |
| MIM-03-AGC-SM-COB-5W/90/35K-D010-UNV | No | 31.62 mm | 3.18 mm  [stored 0.0104331 ft] | 76.2 mm  [stored 0.25 ft] | Yes | AGC-Anthracite gray cord | 03-Warm dark grey painted | 03-Warm dark grey painted | No |
| MIM-03-PWC-SM-COB-5W/90/35K-REM-MC-UNV | No | 15.88 mm  [stored 0.0520997 ft] | 3.18 mm  [stored 0.0104331 ft] | 76.2 mm  [stored 0.25 ft] | No | PWC-Pearly white cord | 03-Warm dark grey painted | 03-Warm dark grey painted | Yes |
| MIM-03-PWC-MD-COB-5W/90/35K-REM-MC-UNV | No | 15.88 mm  [stored 0.0520997 ft] | 3.18 mm  [stored 0.0104331 ft] | 165.1 mm  [stored 0.541667 ft] | No | PWC-Pearly white cord | 03-Warm dark grey painted | 03-Warm dark grey painted | Yes |
| MIM-03-PWC-LG-COB-5W/90/35K-REM-MC-UNV | No | 15.88 mm  [stored 0.0520997 ft] | 3.18 mm  [stored 0.0104331 ft] | 317.5 mm | No | PWC-Pearly white cord | 03-Warm dark grey painted | 03-Warm dark grey painted | Yes |
| MIM-03-PWC-LG-COB-5W/90/35K-D010-UNV | No | 31.62 mm | 3.18 mm  [stored 0.0104331 ft] | 317.5 mm | Yes | PWC-Pearly white cord | 03-Warm dark grey painted | 03-Warm dark grey painted | No |
| MIM-03-PWC-MD-COB-5W/90/35K-D010-UNV | No | 31.62 mm | 3.18 mm  [stored 0.0104331 ft] | 165.1 mm  [stored 0.541667 ft] | Yes | PWC-Pearly white cord | 03-Warm dark grey painted | 03-Warm dark grey painted | No |
| MIM-03-PWC-SM-COB-5W/90/35K-D010-UNV | No | 31.62 mm | 3.18 mm  [stored 0.0104331 ft] | 76.2 mm  [stored 0.25 ft] | Yes | PWC-Pearly white cord | 03-Warm dark grey painted | 03-Warm dark grey painted | No |
| MIM-02-SGC-SM-COB-5W/90/35K-REM-MC-UNV | No | 15.88 mm  [stored 0.0520997 ft] | 3.18 mm  [stored 0.0104331 ft] | 76.2 mm  [stored 0.25 ft] | No | SGC-Satin gold cord | 02-Black painted | 02-Black painted | Yes |
| MIM-02-SGC-MD-COB-5W/90/35K-REM-MC-UNV | No | 15.88 mm  [stored 0.0520997 ft] | 3.18 mm  [stored 0.0104331 ft] | 165.1 mm  [stored 0.541667 ft] | No | SGC-Satin gold cord | 02-Black painted | 02-Black painted | Yes |
| MIM-02-SGC-LG-COB-5W/90/35K-REM-MC-UNV | No | 15.88 mm  [stored 0.0520997 ft] | 3.18 mm  [stored 0.0104331 ft] | 317.5 mm | No | SGC-Satin gold cord | 02-Black painted | 02-Black painted | Yes |
| MIM-02-SGC-LG-COB-5W/90/35K-D010-UNV | No | 31.62 mm | 3.18 mm  [stored 0.0104331 ft] | 317.5 mm | Yes | SGC-Satin gold cord | 02-Black painted | 02-Black painted | No |
| MIM-02-SGC-MD-COB-5W/90/35K-D010-UNV | No | 31.62 mm | 3.18 mm  [stored 0.0104331 ft] | 165.1 mm  [stored 0.541667 ft] | Yes | SGC-Satin gold cord | 02-Black painted | 02-Black painted | No |
| MIM-02-SGC-SM-COB-5W/90/35K-D010-UNV | No | 31.62 mm | 3.18 mm  [stored 0.0104331 ft] | 76.2 mm  [stored 0.25 ft] | Yes | SGC-Satin gold cord | 02-Black painted | 02-Black painted | No |
| MIM-02-SBC-SM-COB-5W/90/35K-REM-MC-UNV | No | 15.88 mm  [stored 0.0520997 ft] | 3.18 mm  [stored 0.0104331 ft] | 76.2 mm  [stored 0.25 ft] | No | SBC-Silky black cord | 02-Black painted | 02-Black painted | Yes |
| MIM-02-SBC-MD-COB-5W/90/35K-REM-MC-UNV | No | 15.88 mm  [stored 0.0520997 ft] | 3.18 mm  [stored 0.0104331 ft] | 165.1 mm  [stored 0.541667 ft] | No | SBC-Silky black cord | 02-Black painted | 02-Black painted | Yes |
| MIM-02-SBC-LG-COB-5W/90/35K-REM-MC-UNV | No | 15.88 mm  [stored 0.0520997 ft] | 3.18 mm  [stored 0.0104331 ft] | 317.5 mm | No | SBC-Silky black cord | 02-Black painted | 02-Black painted | Yes |
| MIM-02-SBC-LG-COB-5W/90/35K-D010-UNV | No | 31.62 mm | 3.18 mm  [stored 0.0104331 ft] | 317.5 mm | Yes | SBC-Silky black cord | 02-Black painted | 02-Black painted | No |
| MIM-02-SBC-MD-COB-5W/90/35K-D010-UNV | No | 31.62 mm | 3.18 mm  [stored 0.0104331 ft] | 165.1 mm  [stored 0.541667 ft] | Yes | SBC-Silky black cord | 02-Black painted | 02-Black painted | No |
| MIM-02-SBC-SM-COB-5W/90/35K-D010-UNV | No | 31.62 mm | 3.18 mm  [stored 0.0104331 ft] | 76.2 mm  [stored 0.25 ft] | Yes | SBC-Silky black cord | 02-Black painted | 02-Black painted | No |
| MIM-02-COC-SM-COB-5W/90/35K-REM-MC-UNV | Yes | 15.88 mm  [stored 0.0520997 ft] | 1.59 mm  [stored 0.00521653 ft] | 76.2 mm  [stored 0.25 ft] | No | COC-Coaxial cable | 02-Black painted | 02-Black painted | Yes |
| MIM-02-COC-MD-COB-5W/90/35K-REM-MC-UNV | Yes | 15.88 mm  [stored 0.0520997 ft] | 1.59 mm  [stored 0.00521653 ft] | 165.1 mm  [stored 0.541667 ft] | No | COC-Coaxial cable | 02-Black painted | 02-Black painted | Yes |
| MIM-02-COC-LG-COB-5W/90/35K-REM-MC-UNV | Yes | 15.88 mm  [stored 0.0520997 ft] | 1.59 mm  [stored 0.00521653 ft] | 317.5 mm | No | COC-Coaxial cable | 02-Black painted | 02-Black painted | Yes |
| MIM-02-COC-LG-COB-5W/90/35K-D010-UNV | Yes | 31.62 mm | 1.59 mm  [stored 0.00521653 ft] | 317.5 mm | Yes | COC-Coaxial cable | 02-Black painted | 02-Black painted | No |
| MIM-02-COC-MD-COB-5W/90/35K-D010-UNV | Yes | 31.62 mm | 1.59 mm  [stored 0.00521653 ft] | 165.1 mm  [stored 0.541667 ft] | Yes | COC-Coaxial cable | 02-Black painted | 02-Black painted | No |
| MIM-02-COC-SM-COB-5W/90/35K-D010-UNV | Yes | 31.62 mm | 1.59 mm  [stored 0.00521653 ft] | 76.2 mm  [stored 0.25 ft] | Yes | COC-Coaxial cable | 02-Black painted | 02-Black painted | No |
| MIM-02-AGC-SM-COB-5W/90/35K-REM-MC-UNV | No | 15.88 mm  [stored 0.0520997 ft] | 3.18 mm  [stored 0.0104331 ft] | 76.2 mm  [stored 0.25 ft] | No | AGC-Anthracite gray cord | 02-Black painted | 02-Black painted | Yes |
| MIM-02-AGC-MD-COB-5W/90/35K-REM-MC-UNV | No | 15.88 mm  [stored 0.0520997 ft] | 3.18 mm  [stored 0.0104331 ft] | 165.1 mm  [stored 0.541667 ft] | No | AGC-Anthracite gray cord | 02-Black painted | 02-Black painted | Yes |
| MIM-02-AGC-LG-COB-5W/90/35K-REM-MC-UNV | No | 15.88 mm  [stored 0.0520997 ft] | 3.18 mm  [stored 0.0104331 ft] | 317.5 mm | No | AGC-Anthracite gray cord | 02-Black painted | 02-Black painted | Yes |
| MIM-02-AGC-LG-COB-5W/90/35K-D010-UNV | No | 31.62 mm | 3.18 mm  [stored 0.0104331 ft] | 317.5 mm | Yes | AGC-Anthracite gray cord | 02-Black painted | 02-Black painted | No |
| MIM-02-AGC-MD-COB-5W/90/35K-D010-UNV | No | 31.62 mm | 3.18 mm  [stored 0.0104331 ft] | 165.1 mm  [stored 0.541667 ft] | Yes | AGC-Anthracite gray cord | 02-Black painted | 02-Black painted | No |
| MIM-02-AGC-SM-COB-5W/90/35K-D010-UNV | No | 31.62 mm | 3.18 mm  [stored 0.0104331 ft] | 76.2 mm  [stored 0.25 ft] | Yes | AGC-Anthracite gray cord | 02-Black painted | 02-Black painted | No |
| MIM-02-PWC-SM-COB-5W/90/35K-REM-MC-UNV | No | 15.88 mm  [stored 0.0520997 ft] | 3.18 mm  [stored 0.0104331 ft] | 76.2 mm  [stored 0.25 ft] | No | PWC-Pearly white cord | 02-Black painted | 02-Black painted | Yes |
| MIM-02-PWC-MD-COB-5W/90/35K-REM-MC-UNV | No | 15.88 mm  [stored 0.0520997 ft] | 3.18 mm  [stored 0.0104331 ft] | 165.1 mm  [stored 0.541667 ft] | No | PWC-Pearly white cord | 02-Black painted | 02-Black painted | Yes |
| MIM-02-PWC-LG-COB-5W/90/35K-REM-MC-UNV | No | 15.88 mm  [stored 0.0520997 ft] | 3.18 mm  [stored 0.0104331 ft] | 317.5 mm | No | PWC-Pearly white cord | 02-Black painted | 02-Black painted | Yes |
| MIM-02-PWC-LG-COB-5W/90/35K-D010-UNV | No | 31.62 mm | 3.18 mm  [stored 0.0104331 ft] | 317.5 mm | Yes | PWC-Pearly white cord | 02-Black painted | 02-Black painted | No |
| MIM-02-PWC-MD-COB-5W/90/35K-D010-UNV | No | 31.62 mm | 3.18 mm  [stored 0.0104331 ft] | 165.1 mm  [stored 0.541667 ft] | Yes | PWC-Pearly white cord | 02-Black painted | 02-Black painted | No |
| MIM-02-PWC-SM-COB-5W/90/35K-D010-UNV | No | 31.62 mm | 3.18 mm  [stored 0.0104331 ft] | 76.2 mm  [stored 0.25 ft] | Yes | PWC-Pearly white cord | 02-Black painted | 02-Black painted | No |
| MIM-01-SGC-SM-COB-5W/90/35K-REM-MC-UNV | No | 15.88 mm  [stored 0.0520997 ft] | 3.18 mm  [stored 0.0104331 ft] | 76.2 mm  [stored 0.25 ft] | No | SGC-Satin gold cord | 01-White painted | 01-White painted | Yes |
| MIM-01-SGC-MD-COB-5W/90/35K-REM-MC-UNV | No | 15.88 mm  [stored 0.0520997 ft] | 3.18 mm  [stored 0.0104331 ft] | 165.1 mm  [stored 0.541667 ft] | No | SGC-Satin gold cord | 01-White painted | 01-White painted | Yes |
| MIM-01-SGC-LG-COB-5W/90/35K-REM-MC-UNV | No | 15.88 mm  [stored 0.0520997 ft] | 3.18 mm  [stored 0.0104331 ft] | 317.5 mm | No | SGC-Satin gold cord | 01-White painted | 01-White painted | Yes |
| MIM-01-SGC-LG-COB-5W/90/35K-D010-UNV | No | 31.62 mm | 3.18 mm  [stored 0.0104331 ft] | 317.5 mm | Yes | SGC-Satin gold cord | 01-White painted | 01-White painted | No |
| MIM-01-SGC-MD-COB-5W/90/35K-D010-UNV | No | 31.62 mm | 3.18 mm  [stored 0.0104331 ft] | 165.1 mm  [stored 0.541667 ft] | Yes | SGC-Satin gold cord | 01-White painted | 01-White painted | No |
| MIM-01-SGC-SM-COB-5W/90/35K-D010-UNV | No | 31.62 mm | 3.18 mm  [stored 0.0104331 ft] | 76.2 mm  [stored 0.25 ft] | Yes | SGC-Satin gold cord | 01-White painted | 01-White painted | No |
| MIM-01-SBC-SM-COB-5W/90/35K-REM-MC-UNV | No | 15.88 mm  [stored 0.0520997 ft] | 3.18 mm  [stored 0.0104331 ft] | 76.2 mm  [stored 0.25 ft] | No | SBC-Silky black cord | 01-White painted | 01-White painted | Yes |
| MIM-01-SBC-MD-COB-5W/90/35K-REM-MC-UNV | No | 15.88 mm  [stored 0.0520997 ft] | 3.18 mm  [stored 0.0104331 ft] | 165.1 mm  [stored 0.541667 ft] | No | SBC-Silky black cord | 01-White painted | 01-White painted | Yes |
| MIM-01-SBC-LG-COB-5W/90/35K-REM-MC-UNV | No | 15.88 mm  [stored 0.0520997 ft] | 3.18 mm  [stored 0.0104331 ft] | 317.5 mm | No | SBC-Silky black cord | 01-White painted | 01-White painted | Yes |
| MIM-01-SBC-LG-COB-5W/90/35K-D010-UNV | No | 31.62 mm | 3.18 mm  [stored 0.0104331 ft] | 317.5 mm | Yes | SBC-Silky black cord | 01-White painted | 01-White painted | No |
| MIM-01-SBC-MD-COB-5W/90/35K-D010-UNV | No | 31.62 mm | 3.18 mm  [stored 0.0104331 ft] | 165.1 mm  [stored 0.541667 ft] | Yes | SBC-Silky black cord | 01-White painted | 01-White painted | No |
| MIM-01-SBC-SM-COB-5W/90/35K-D010-UNV | No | 31.62 mm | 3.18 mm  [stored 0.0104331 ft] | 76.2 mm  [stored 0.25 ft] | Yes | SBC-Silky black cord | 01-White painted | 01-White painted | No |
| MIM-01-COC-SM-COB-5W/90/35K-REM-MC-UNV | Yes | 15.88 mm  [stored 0.0520997 ft] | 1.59 mm  [stored 0.00521653 ft] | 76.2 mm  [stored 0.25 ft] | No | COC-Coaxial cable | 01-White painted | 01-White painted | Yes |
| MIM-01-COC-MD-COB-5W/90/35K-REM-MC-UNV | Yes | 15.88 mm  [stored 0.0520997 ft] | 1.59 mm  [stored 0.00521653 ft] | 165.1 mm  [stored 0.541667 ft] | No | COC-Coaxial cable | 01-White painted | 01-White painted | Yes |
| MIM-01-COC-LG-COB-5W/90/35K-REM-MC-UNV | Yes | 15.88 mm  [stored 0.0520997 ft] | 1.59 mm  [stored 0.00521653 ft] | 317.5 mm | No | COC-Coaxial cable | 01-White painted | 01-White painted | Yes |
| MIM-01-COC-LG-COB-5W/90/35K-D010-UNV | Yes | 31.62 mm | 1.59 mm  [stored 0.00521653 ft] | 317.5 mm | Yes | COC-Coaxial cable | 01-White painted | 01-White painted | No |
| MIM-01-COC-MD-COB-5W/90/35K-D010-UNV | Yes | 31.62 mm | 1.59 mm  [stored 0.00521653 ft] | 165.1 mm  [stored 0.541667 ft] | Yes | COC-Coaxial cable | 01-White painted | 01-White painted | No |
| MIM-01-COC-SM-COB-5W/90/35K-D010-UNV | Yes | 31.62 mm | 1.59 mm  [stored 0.00521653 ft] | 76.2 mm  [stored 0.25 ft] | Yes | COC-Coaxial cable | 01-White painted | 01-White painted | No |
| MIM-01-AGC-SM-COB-5W/90/35K-REM-MC-UNV | No | 15.88 mm  [stored 0.0520997 ft] | 3.18 mm  [stored 0.0104331 ft] | 76.2 mm  [stored 0.25 ft] | No | AGC-Anthracite gray cord | 01-White painted | 01-White painted | Yes |
| MIM-01-AGC-MD-COB-5W/90/35K-REM-MC-UNV | No | 15.88 mm  [stored 0.0520997 ft] | 3.18 mm  [stored 0.0104331 ft] | 165.1 mm  [stored 0.541667 ft] | No | AGC-Anthracite gray cord | 01-White painted | 01-White painted | Yes |
| MIM-01-AGC-LG-COB-5W/90/35K-REM-MC-UNV | No | 15.88 mm  [stored 0.0520997 ft] | 3.18 mm  [stored 0.0104331 ft] | 317.5 mm | No | AGC-Anthracite gray cord | 01-White painted | 01-White painted | Yes |
| MIM-01-AGC-LG-COB-5W/90/35K-D010-UNV | No | 31.62 mm | 3.18 mm  [stored 0.0104331 ft] | 317.5 mm | Yes | AGC-Anthracite gray cord | 01-White painted | 01-White painted | No |
| MIM-01-AGC-MD-COB-5W/90/35K-D010-UNV | No | 31.62 mm | 3.18 mm  [stored 0.0104331 ft] | 165.1 mm  [stored 0.541667 ft] | Yes | AGC-Anthracite gray cord | 01-White painted | 01-White painted | No |
| MIM-01-AGC-SM-COB-5W/90/35K-D010-UNV | No | 31.62 mm | 3.18 mm  [stored 0.0104331 ft] | 76.2 mm  [stored 0.25 ft] | Yes | AGC-Anthracite gray cord | 01-White painted | 01-White painted | No |
| MIM-01-PWC-SM-COB-5W/90/35K-REM-MC-UNV | No | 15.88 mm  [stored 0.0520997 ft] | 3.18 mm  [stored 0.0104331 ft] | 76.2 mm  [stored 0.25 ft] | No | PWC-Pearly white cord | 01-White painted | 01-White painted | Yes |
| MIM-01-PWC-MD-COB-5W/90/35K-REM-MC-UNV | No | 15.88 mm  [stored 0.0520997 ft] | 3.18 mm  [stored 0.0104331 ft] | 165.1 mm  [stored 0.541667 ft] | No | PWC-Pearly white cord | 01-White painted | 01-White painted | Yes |
| MIM-01-PWC-LG-COB-5W/90/35K-REM-MC-UNV | No | 15.88 mm  [stored 0.0520997 ft] | 3.18 mm  [stored 0.0104331 ft] | 317.5 mm | No | PWC-Pearly white cord | 01-White painted | 01-White painted | Yes |
| MIM-01-PWC-LG-COB-5W/90/35K-D010-UNV | No | 31.62 mm | 3.18 mm  [stored 0.0104331 ft] | 317.5 mm | Yes | PWC-Pearly white cord | 01-White painted | 01-White painted | No |
| MIM-01-PWC-MD-COB-5W/90/35K-D010-UNV | No | 31.62 mm | 3.18 mm  [stored 0.0104331 ft] | 165.1 mm  [stored 0.541667 ft] | Yes | PWC-Pearly white cord | 01-White painted | 01-White painted | No |
| MIM-01-PWC-SM-COB-5W/90/35K-D010-UNV | No | 31.62 mm | 3.18 mm  [stored 0.0104331 ft] | 76.2 mm  [stored 0.25 ft] | Yes | PWC-Pearly white cord | 01-White painted | 01-White painted | No |
| MIM-31-SGC-SM-COB-5W/90/35K-REM-MC-UNV | No | 15.88 mm  [stored 0.0520997 ft] | 3.18 mm  [stored 0.0104331 ft] | 76.2 mm  [stored 0.25 ft] | No | SGC-Satin gold cord | 31-Polished nickel plated | 31-Polished nickel plated | Yes |
| MIM-31-SGC-MD-COB-5W/90/35K-REM-MC-UNV | No | 15.88 mm  [stored 0.0520997 ft] | 3.18 mm  [stored 0.0104331 ft] | 165.1 mm  [stored 0.541667 ft] | No | SGC-Satin gold cord | 31-Polished nickel plated | 31-Polished nickel plated | Yes |
| MIM-31-SGC-LG-COB-5W/90/35K-REM-MC-UNV | No | 15.88 mm  [stored 0.0520997 ft] | 3.18 mm  [stored 0.0104331 ft] | 317.5 mm | No | SGC-Satin gold cord | 31-Polished nickel plated | 31-Polished nickel plated | Yes |
| MIM-31-SGC-LG-COB-5W/90/35K-D010-UNV | No | 31.62 mm | 3.18 mm  [stored 0.0104331 ft] | 317.5 mm | Yes | SGC-Satin gold cord | 31-Polished nickel plated | 31-Polished nickel plated | No |
| MIM-31-SGC-MD-COB-5W/90/35K-D010-UNV | No | 31.62 mm | 3.18 mm  [stored 0.0104331 ft] | 165.1 mm  [stored 0.541667 ft] | Yes | SGC-Satin gold cord | 31-Polished nickel plated | 31-Polished nickel plated | No |
| MIM-31-SGC-SM-COB-5W/90/35K-D010-UNV | No | 31.62 mm | 3.18 mm  [stored 0.0104331 ft] | 76.2 mm  [stored 0.25 ft] | Yes | SGC-Satin gold cord | 31-Polished nickel plated | 31-Polished nickel plated | No |
| MIM-31-SBC-SM-COB-5W/90/35K-REM-MC-UNV | No | 15.88 mm  [stored 0.0520997 ft] | 3.18 mm  [stored 0.0104331 ft] | 76.2 mm  [stored 0.25 ft] | No | SBC-Silky black cord | 31-Polished nickel plated | 31-Polished nickel plated | Yes |
| MIM-31-SBC-MD-COB-5W/90/35K-REM-MC-UNV | No | 15.88 mm  [stored 0.0520997 ft] | 3.18 mm  [stored 0.0104331 ft] | 165.1 mm  [stored 0.541667 ft] | No | SBC-Silky black cord | 31-Polished nickel plated | 31-Polished nickel plated | Yes |
| MIM-31-SBC-LG-COB-5W/90/35K-REM-MC-UNV | No | 15.88 mm  [stored 0.0520997 ft] | 3.18 mm  [stored 0.0104331 ft] | 317.5 mm | No | SBC-Silky black cord | 31-Polished nickel plated | 31-Polished nickel plated | Yes |
| MIM-31-SBC-LG-COB-5W/90/35K-D010-UNV | No | 31.62 mm | 3.18 mm  [stored 0.0104331 ft] | 317.5 mm | Yes | SBC-Silky black cord | 31-Polished nickel plated | 31-Polished nickel plated | No |
| MIM-31-SBC-MD-COB-5W/90/35K-D010-UNV | No | 31.62 mm | 3.18 mm  [stored 0.0104331 ft] | 165.1 mm  [stored 0.541667 ft] | Yes | SBC-Silky black cord | 31-Polished nickel plated | 31-Polished nickel plated | No |
| MIM-31-SBC-SM-COB-5W/90/35K-D010-UNV | No | 31.62 mm | 3.18 mm  [stored 0.0104331 ft] | 76.2 mm  [stored 0.25 ft] | Yes | SBC-Silky black cord | 31-Polished nickel plated | 31-Polished nickel plated | No |
| MIM-31-COC-SM-COB-5W/90/35K-REM-MC-UNV | Yes | 15.88 mm  [stored 0.0520997 ft] | 1.59 mm  [stored 0.00521653 ft] | 76.2 mm  [stored 0.25 ft] | No | COC-Coaxial cable | 31-Polished nickel plated | 31-Polished nickel plated | Yes |
| MIM-31-COC-MD-COB-5W/90/35K-REM-MC-UNV | Yes | 15.88 mm  [stored 0.0520997 ft] | 1.59 mm  [stored 0.00521653 ft] | 165.1 mm  [stored 0.541667 ft] | No | COC-Coaxial cable | 31-Polished nickel plated | 31-Polished nickel plated | Yes |
| MIM-31-COC-LG-COB-5W/90/35K-REM-MC-UNV | Yes | 15.88 mm  [stored 0.0520997 ft] | 1.59 mm  [stored 0.00521653 ft] | 317.5 mm | No | COC-Coaxial cable | 31-Polished nickel plated | 31-Polished nickel plated | Yes |
| MIM-31-COC-LG-COB-5W/90/35K-D010-UNV | Yes | 31.62 mm | 1.59 mm  [stored 0.00521653 ft] | 317.5 mm | Yes | COC-Coaxial cable | 31-Polished nickel plated | 31-Polished nickel plated | No |
| MIM-31-COC-MD-COB-5W/90/35K-D010-UNV | Yes | 31.62 mm | 1.59 mm  [stored 0.00521653 ft] | 165.1 mm  [stored 0.541667 ft] | Yes | COC-Coaxial cable | 31-Polished nickel plated | 31-Polished nickel plated | No |
| MIM-31-COC-SM-COB-5W/90/35K-D010-UNV | Yes | 31.62 mm | 1.59 mm  [stored 0.00521653 ft] | 76.2 mm  [stored 0.25 ft] | Yes | COC-Coaxial cable | 31-Polished nickel plated | 31-Polished nickel plated | No |
| MIM-31-AGC-SM-COB-5W/90/35K-REM-MC-UNV | No | 15.88 mm  [stored 0.0520997 ft] | 3.18 mm  [stored 0.0104331 ft] | 76.2 mm  [stored 0.25 ft] | No | AGC-Anthracite gray cord | 31-Polished nickel plated | 31-Polished nickel plated | Yes |
| MIM-31-AGC-MD-COB-5W/90/35K-REM-MC-UNV | No | 15.88 mm  [stored 0.0520997 ft] | 3.18 mm  [stored 0.0104331 ft] | 165.1 mm  [stored 0.541667 ft] | No | AGC-Anthracite gray cord | 31-Polished nickel plated | 31-Polished nickel plated | Yes |
| MIM-31-AGC-LG-COB-5W/90/35K-REM-MC-UNV | No | 15.88 mm  [stored 0.0520997 ft] | 3.18 mm  [stored 0.0104331 ft] | 317.5 mm | No | AGC-Anthracite gray cord | 31-Polished nickel plated | 31-Polished nickel plated | Yes |
| MIM-31-AGC-LG-COB-5W/90/35K-D010-UNV | No | 31.62 mm | 3.18 mm  [stored 0.0104331 ft] | 317.5 mm | Yes | AGC-Anthracite gray cord | 31-Polished nickel plated | 31-Polished nickel plated | No |
| MIM-31-AGC-MD-COB-5W/90/35K-D010-UNV | No | 31.62 mm | 3.18 mm  [stored 0.0104331 ft] | 165.1 mm  [stored 0.541667 ft] | Yes | AGC-Anthracite gray cord | 31-Polished nickel plated | 31-Polished nickel plated | No |
| MIM-31-AGC-SM-COB-5W/90/35K-D010-UNV | No | 31.62 mm | 3.18 mm  [stored 0.0104331 ft] | 76.2 mm  [stored 0.25 ft] | Yes | AGC-Anthracite gray cord | 31-Polished nickel plated | 31-Polished nickel plated | No |

note: column(s) folded — value = type name in every type: HL_FeatureCode

note: [stored X ft] marks values corroborated as IEEE doubles in the binary element streams (Revit-internal decimal feet)

## geometry (parser evidence)
native form markers: Sweep x2
no freeform markers — native parametric forms only
